# Revit family: LB6LEDA10L
name_source: partatom
category: Lighting Fixtures
revit_build: Autodesk Revit Architecture 2012 (Build: 20110309_2315(x64)
units: mm (PartAtom-declared; Revit-internal decimal feet)

## types (4) — shared parameters
Color Filter = 16777215
Default Elevation = 48"
Description = 6inch LED DOWNLIGHT MODULE
Dimming Lamp Color Temperature Shift = <None>
Emit from Line Length = 24"
Flange = Aluminum
Lamp = LED
Manufacturer = Prescolite
Manufacturer Fax = (866)-898-1065
Model = LB6LEDA10L
Product Documentation Link = http://www.prescolite.com
Product Page URL = http://www.prescolite.com
Steel = Steel
Tilt Angle = -90.00°
URL = www.prescolite.com
Wattage Comments = 12W

## per-type parameters (varying)
| type | Photometric Web File | Voltage |
| 6" LiteBox 1000 Lumen 27K LED w/15% dimming | 6184.ies | 0 V |
| 6" LiteBox 1000 Lumen 35K LED w/15% dimming | 6182.ies | 0 V |
| 6" LiteBox LED Downlight LB6LEDA8L30K WH | lb6leda8l30kwh.ies | 120 V |
| 6" LiteBox 1000 Lumen 30K LED w/15% dimming | 6183.ies | 0 V |

## geometry (parser evidence)
native form markers: Sweep x1
no freeform markers — native parametric forms only
